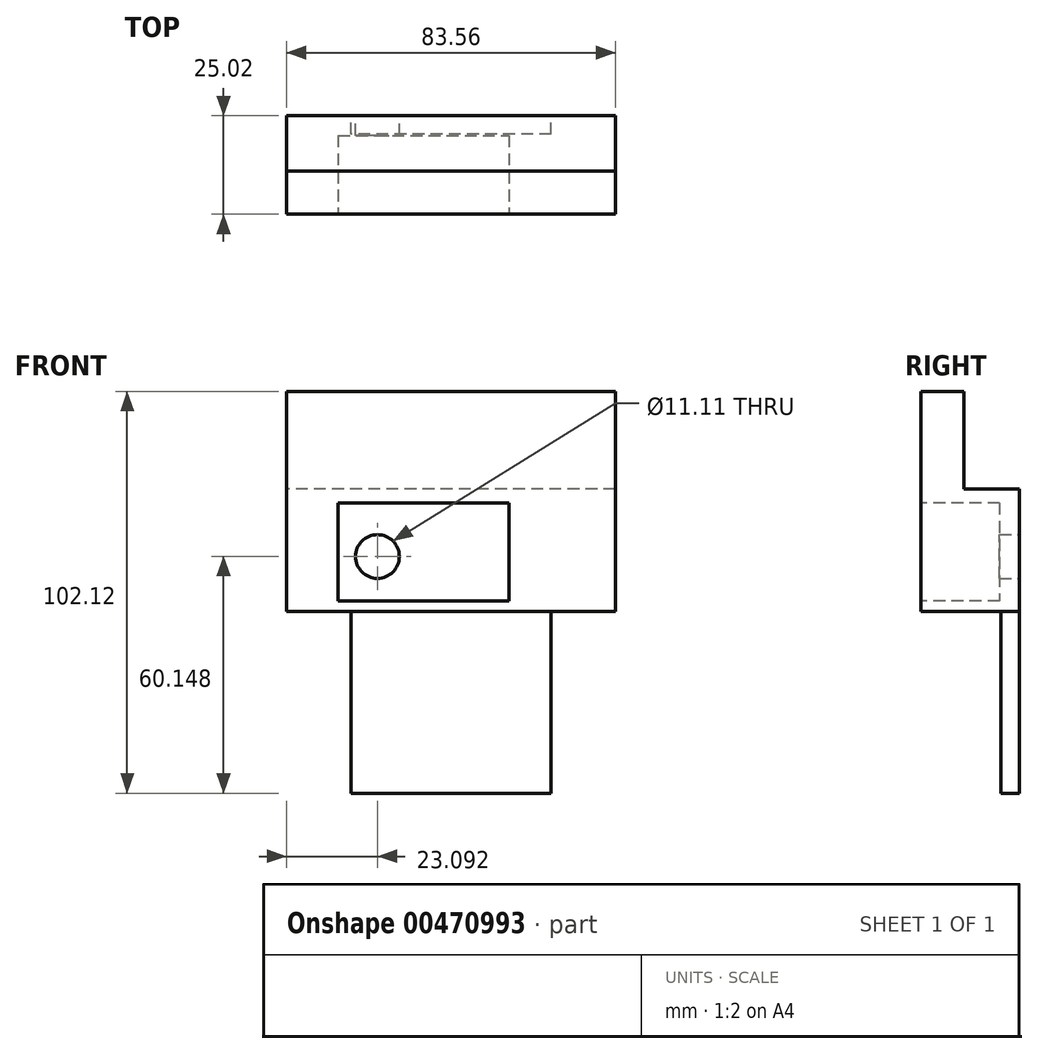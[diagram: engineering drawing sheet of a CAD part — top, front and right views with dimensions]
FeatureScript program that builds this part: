
annotation { "Feature Type Name" : "Feature", "Feature Type Description" : "" }
export const myFeature = defineFeature(function(context is Context, id is Id, definition is map)
    precondition{}
    {
        {
            var Q0;
            Q0=qCreatedBy(makeId("Front.planeOp"),FACE);
            var sketch = newSketch(context, id + "F0", { "sketchPlane" : qUnion([Q0])});
            skLineSegment(sketch, "E0.bottom", {"start": v(41.78, 27.98) * mm, "end": v(-41.78, 27.98) * mm});
            skLineSegment(sketch, "E0.top", {"start": v(41.78, -27.98) * mm, "end": v(-41.78, -27.98) * mm});
            skLineSegment(sketch, "E0.left", {"start": v(41.78, 27.98) * mm, "end": v(41.78, -27.98) * mm});
            skLineSegment(sketch, "E0.right", {"start": v(-41.78, 27.98) * mm, "end": v(-41.78, -27.98) * mm});
            skPoint(sketch, "E0.middle", {"position": v(0, 0) * mm});
            skSolve(sketch);
        }
        {
            var Q0;
            Q0=makeQuery(id+"F0.imprint","IMPRINT",FACE,{"disambiguationData":[TD([[makeQuery(id+"F0.imprint","IMPRINT",EDGE,{"derivedFrom":sQuery(id+"F0.wireOp",EDGE,"E0.bottom")}),1.0]])]});
            extrude(context, id + "F1", {"entities" : qUnion([Q0]), "depth" : 10.9 * mm});
        }
        {
            var Q0;
            Q0=makeQuery(id+"F1.opExtrude","CAP_FACE",FACE,{"disambiguationData":[OSD([sQuery(id+"F0.wireOp",EDGE,"E0.bottom"),sQuery(id+"F0.wireOp",EDGE,"E0.top"),sQuery(id+"F0.wireOp",EDGE,"E0.left"),sQuery(id+"F0.wireOp",EDGE,"E0.right")])],"isStart":true});
            var sketch = newSketch(context, id + "F2", { "sketchPlane" : qUnion([Q0])});
            skLineSegment(sketch, "E1.bottom", {"start": v(-41.78, -27.98) * mm, "end": v(41.78, -27.98) * mm});
            skLineSegment(sketch, "E1.top", {"start": v(-41.78, 3.17) * mm, "end": v(41.78, 3.17) * mm});
            skLineSegment(sketch, "E1.left", {"start": v(-41.78, -27.98) * mm, "end": v(-41.78, 3.17) * mm});
            skLineSegment(sketch, "E1.right", {"start": v(41.78, -27.98) * mm, "end": v(41.78, 3.17) * mm});
            skSolve(sketch);
        }
        {
            var Q0;
            Q0 = qSketchRegion(id + "F2", true);
            extrude(context, id + "F3", {"entities" : qUnion([Q0]), "operationType" : NewBodyOperationType.ADD, "depth" : 14.1 * mm});
        }
        {
            var Q0;
            Q0=makeQuery(id+"F3.opExtrude","CAP_FACE",FACE,{"disambiguationData":[OSD([sQuery(id+"F2.wireOp",EDGE,"E1.bottom"),sQuery(id+"F2.wireOp",EDGE,"E1.top"),sQuery(id+"F2.wireOp",EDGE,"E1.left"),sQuery(id+"F2.wireOp",EDGE,"E1.right")])],"isStart":false});
            var sketch = newSketch(context, id + "F4", { "sketchPlane" : qUnion([Q0])});
            skLineSegment(sketch, "E2.bottom", {"start": v(-25.45, -27.98) * mm, "end": v(25.44, -27.98) * mm});
            skLineSegment(sketch, "E2.top", {"start": v(-25.45, -74.14) * mm, "end": v(25.44, -74.14) * mm});
            skLineSegment(sketch, "E2.left", {"start": v(-25.45, -27.98) * mm, "end": v(-25.45, -74.14) * mm});
            skLineSegment(sketch, "E2.right", {"start": v(25.44, -27.98) * mm, "end": v(25.44, -74.14) * mm});
            skSolve(sketch);
        }
        {
            var Q0;
            Q0=makeQuery(id+"F4.imprint","IMPRINT",FACE,{"disambiguationData":[TD([[makeQuery(id+"F4.imprint","IMPRINT",EDGE,{"derivedFrom":sQuery(id+"F4.wireOp",EDGE,"E2.bottom")}),-1.0]])]});
            extrude(context, id + "F5", {"entities" : qUnion([Q0]), "operationType" : NewBodyOperationType.ADD, "oppositeDirection" : true, "depth" : 4.7 * mm});
        }
        {
            var Q0;
            Q0=makeQuery(id+"F1.opExtrude","CAP_FACE",FACE,{"disambiguationData":[OSD([sQuery(id+"F0.wireOp",EDGE,"E0.bottom"),sQuery(id+"F0.wireOp",EDGE,"E0.top"),sQuery(id+"F0.wireOp",EDGE,"E0.left"),sQuery(id+"F0.wireOp",EDGE,"E0.right")])],"isStart":false});
            var sketch = newSketch(context, id + "F6", { "sketchPlane" : qUnion([Q0])});
            skLineSegment(sketch, "E3", {"start": v(-28.69, 27.98) * mm, "end": v(-28.69, -27.98) * mm});
            skLineSegment(sketch, "E4", {"start": v(-28.69, -25.28) * mm, "end": v(41.78, -25.28) * mm});
            skLineSegment(sketch, "E5", {"start": v(-28.69, -0.36) * mm, "end": v(41.78, -0.36) * mm});
            skLineSegment(sketch, "E6", {"start": v(14.7, -0.36) * mm, "end": v(14.7, -25.28) * mm});
            skSolve(sketch);
        }
        {
            var Q0;
            {var subQ5=sQuery(id+"F6.wireOp",EDGE,"E6");Q0=makeQuery(id+"F6.imprint","IMPRINT",FACE,{"disambiguationData":[TD([[makeQuery(id+"F6.imprint","IMPRINT",EDGE,{"derivedFrom":subQ5}),-1.0]])]});}
            extrude(context, id + "F7", {"entities" : qUnion([Q0]), "operationType" : NewBodyOperationType.REMOVE, "oppositeDirection" : true, "depth" : 20.02 * mm});
        }
        {
            var Q0;
            Q0=makeQuery(id+"F5.boolean.opBoolean","MERGE",FACE,{"derivedFrom":[makeQuery(id+"F3.opExtrude","CAP_FACE",FACE,{"disambiguationData":[OSD([sQuery(id+"F2.wireOp",EDGE,"E1.bottom"),sQuery(id+"F2.wireOp",EDGE,"E1.top"),sQuery(id+"F2.wireOp",EDGE,"E1.left"),sQuery(id+"F2.wireOp",EDGE,"E1.right")])],"isStart":false}),makeQuery(id+"F5.opExtrude","CAP_FACE",FACE,{"disambiguationData":[OSD([sQuery(id+"F4.wireOp",EDGE,"E2.bottom"),sQuery(id+"F4.wireOp",EDGE,"E2.top"),sQuery(id+"F4.wireOp",EDGE,"E2.left"),sQuery(id+"F4.wireOp",EDGE,"E2.right")])],"isStart":true})]});
            var sketch = newSketch(context, id + "F8", { "sketchPlane" : qUnion([Q0])});
            skCircle(sketch, "E7", {"center": v(18.69, -14) * mm, "radius": 5.56 * mm});
            skSolve(sketch);
        }
        {
            var Q0;
            Q0 = qSketchRegion(id + "F8", true);
            extrude(context, id + "F9", {"entities" : qUnion([Q0]), "operationType" : NewBodyOperationType.REMOVE, "oppositeDirection" : true, "depth" : 25.4 * mm});
        }
    });
